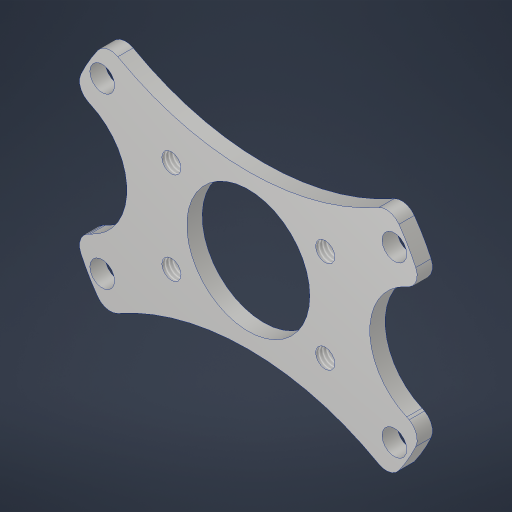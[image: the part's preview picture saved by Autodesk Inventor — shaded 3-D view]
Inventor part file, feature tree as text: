
AUTODESK INVENTOR PART (.ipt)
format: ipt  version: 2023.4 (Build 274418000, 418)  size: 344,064 bytes
history: native  units: in
note: dims shown in document units (in); Inventor stores cm internally (conversion verified against a paired STEP export)
features: sketch x5, extrude x4, hole x2, fillet x1, thicken_offset x1, projected_geometry x1
ambient origin geometry x8: Origin, YZ Plane, XZ Plane, XY Plane, X Axis, Y Axis, Z Axis, Center Point
bodies: Solid1 (feature_tree)
feature tree (14):
  sketch  "Sketch1"  dims[d0=2.375in d1=1.375in d2=0.5in]
  extrude  "Extrusion1"  Depth=1.375in
  fillet  "Fillet1"  Radius=0.5in
  hole  "Hole1"  [1 undecoded]
  extrude  "Extrusion2"  Depth=0.5in
  hole  "Hole2"  [1 undecoded]
  extrude  "Extrusion3"  Depth=0.125in
  extrude  "Extrusion4"  Depth=0.25in TaperAngle=0.0deg
  thicken_offset  "Thicken1"
  sketch  "Sketch3"  dims[d3=0.5in d4=0.5in]
  sketch  "Sketch4"  dims[d5=0.5in d6=1.25in]
  sketch  "Sketch5"  dims[d7=0.5in d8=0.5in]
  sketch  "Sketch6"  dims[d9=0.125in d10=0.125in d11=0.75in d12=0.0in d13=0.125in d14=0.201in d15=0.75in d16=0.385in d17=0.25in d18=0.5635in d19=1.0in d20=0.8108in d21=1.885in d22=0.125in d23=0.0in d24=0.125in d25=0.125in d26=0.125in d27=3.0in d28=1.0in d29=1.25in d30=0.75in d31=0.156in d32=0.38in d33=0.119in d34=0.25in d35=0.5635in d36=1.0in d37=0.8108in d38=2.25in d39=0.6875in d40=0.0in d41=0.8999in d42=0.0in d43=0.0625in d44=0.0625in]
  projected_geometry  "Project Cut Edges1"
note: 2 required parameter values undecoded (feature->parameter linkage not recoverable at this tier; creation-order binding heuristic only, values carry confidence <= 0.55)
